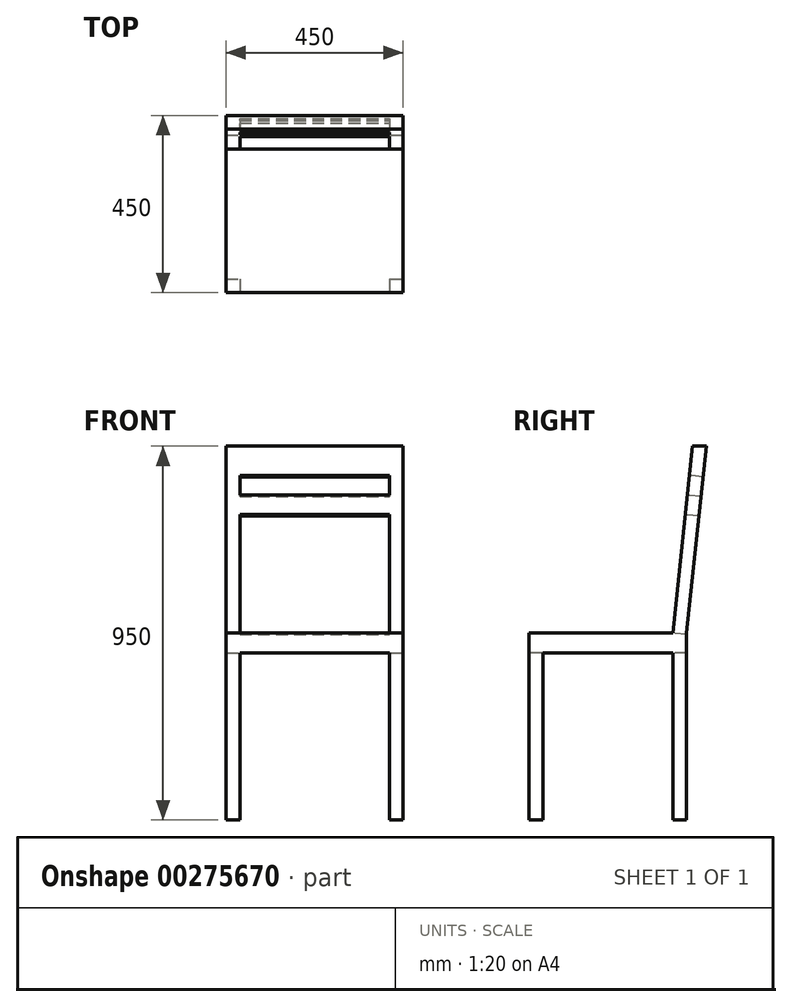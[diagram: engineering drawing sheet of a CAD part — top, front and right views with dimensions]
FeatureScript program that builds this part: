
annotation { "Feature Type Name" : "Feature", "Feature Type Description" : "" }
export const myFeature = defineFeature(function(context is Context, id is Id, definition is map)
    precondition{}
    {
        {
            var Q0;
            Q0=qCreatedBy(makeId("Top.planeOp"),FACE);
            var sketch = newSketch(context, id + "F0", { "sketchPlane" : qUnion([Q0])});
            skLineSegment(sketch, "E0.bottom", {"start": v(225, 225) * mm, "end": v(-225, 225) * mm});
            skLineSegment(sketch, "E0.top", {"start": v(225, -225) * mm, "end": v(-225, -225) * mm});
            skLineSegment(sketch, "E0.left", {"start": v(225, 225) * mm, "end": v(225, -225) * mm});
            skLineSegment(sketch, "E0.right", {"start": v(-225, 225) * mm, "end": v(-225, -225) * mm});
            skPoint(sketch, "E0.middle", {"position": v(0, 0) * mm});
            skSolve(sketch);
        }
        {
            var Q0;
            Q0=qSketchRegion(id+"F0",true);
            extrude(context, id + "F1", {"entities" : qUnion([Q0]), "depth" : 950 * mm});
        }
        {
            var Q0;
            Q0=makeQuery(id+"F1.opExtrude","SWEPT_FACE",FACE,{"disambiguationData":[OSD([sQuery(id+"F0.wireOp",EDGE,"E0.left")])]});
            var sketch = newSketch(context, id + "F2", { "sketchPlane" : qUnion([Q0])});
            skLineSegment(sketch, "E1.bottom", {"start": v(225, 475) * mm, "end": v(-225, 475) * mm});
            skLineSegment(sketch, "E1.top", {"start": v(225, 425) * mm, "end": v(-225, 425) * mm});
            skLineSegment(sketch, "E1.left", {"start": v(225, 475) * mm, "end": v(225, 425) * mm});
            skLineSegment(sketch, "E1.right", {"start": v(-225, 475) * mm, "end": v(-225, 425) * mm});
            skLineSegment(sketch, "E2", {"start": v(225, 950) * mm, "end": v(175, 475) * mm});
            skLineSegment(sketch, "E3", {"start": v(190, 950) * mm, "end": v(140, 475) * mm});
            skLineSegment(sketch, "E4", {"start": v(175, 475) * mm, "end": v(175, 0) * mm});
            skLineSegment(sketch, "E5", {"start": v(140, 475) * mm, "end": v(140, 0) * mm});
            skLineSegment(sketch, "E6", {"start": v(-190, 425) * mm, "end": v(-190, 0) * mm});
            skSolve(sketch);
        }
        {
            var Q0;
            {var subQ0=sQuery(id+"F2.wireOp",EDGE,"E1.left");Q0=makeQuery(id+"F2.imprint","IMPRINT",FACE,{"disambiguationData":[TD([[makeQuery(id+"F2.imprint","IMPRINT",EDGE,{"derivedFrom":subQ0}),-1.0]])]});}
            var Q1;
            {var subQ4=sQuery(id+"F2.wireOp",EDGE,"E2");Q1=makeQuery(id+"F2.imprint","IMPRINT",FACE,{"disambiguationData":[TD([[makeQuery(id+"F2.imprint","IMPRINT",EDGE,{"derivedFrom":subQ4}),1.0]])]});}
            var Q2;
            {var subQ1=sQuery(id+"F0.wireOp",EDGE,"E0.left");var subQ4=sQuery(id+"F2.wireOp",EDGE,"E4");var subQ6=makeQuery(id+"F1.opExtrude","CAP_EDGE",EDGE,{"disambiguationData":[OSD([subQ1])],"isStart":true});var subQ8=makeQuery(id+"F2.imprint","INTERSECT",VERTEX,{"derivedFrom":[subQ6,subQ4]});Q2=makeQuery(id+"F2.imprint","IMPRINT",FACE,{"disambiguationData":[TD([[makeQuery(id+"F2.imprint","IMPRINT",EDGE,{"disambiguationData":[TD([[subQ8,1.0]])],"derivedFrom":subQ4}),1.0]])]});}
            var Q3;
            {var subQ0=sQuery(id+"F2.wireOp",EDGE,"E6");Q3=makeQuery(id+"F2.imprint","IMPRINT",FACE,{"disambiguationData":[TD([[makeQuery(id+"F2.imprint","IMPRINT",EDGE,{"derivedFrom":subQ0}),1.0]])]});}
            var Q4;
            {var subQ4=sQuery(id+"F2.wireOp",EDGE,"E3");Q4=makeQuery(id+"F2.imprint","IMPRINT",FACE,{"disambiguationData":[TD([[makeQuery(id+"F2.imprint","IMPRINT",EDGE,{"derivedFrom":subQ4}),-1.0]])]});}
            extrude(context, id + "F3", {"entities" : qUnion([Q0, Q1, Q2, Q3, Q4]), "operationType" : NewBodyOperationType.REMOVE, "endBound" : BoundingType.THROUGH_ALL, "oppositeDirection" : true, "depth" : 25 * mm});
        }
        {
            var Q0;
            Q0=makeQuery(id+"F1.opExtrude","SWEPT_FACE",FACE,{"disambiguationData":[OSD([sQuery(id+"F0.wireOp",EDGE,"E0.top")])]});
            var sketch = newSketch(context, id + "F4", { "sketchPlane" : qUnion([Q0])});
            skLineSegment(sketch, "E7", {"start": v(-190, 0) * mm, "end": v(-190, 425) * mm});
            skLineSegment(sketch, "E8", {"start": v(-190, 425) * mm, "end": v(190, 425) * mm});
            skLineSegment(sketch, "E9", {"start": v(190, 425) * mm, "end": v(190, 0) * mm});
            skSolve(sketch);
        }
        {
            var Q0;
            Q0 = qSketchRegion(id + "F4", true);
            var Q1;
            {var subQ0=sQuery(id+"F4.wireOp",EDGE,"E7");Q1=makeQuery(id+"F4.imprint","IMPRINT",FACE,{"disambiguationData":[TD([[makeQuery(id+"F4.imprint","IMPRINT",EDGE,{"derivedFrom":subQ0}),-1.0]])]});}
            extrude(context, id + "F5", {"entities" : qUnion([Q0, Q1]), "operationType" : NewBodyOperationType.REMOVE, "endBound" : BoundingType.THROUGH_ALL, "oppositeDirection" : true, "depth" : 25 * mm});
        }
        {
            var Q0;
            Q0=makeQuery(id+"F3.boolean.opBoolean","COPY",FACE,{"derivedFrom":makeQuery(id+"F3.opExtrude","SWEPT_FACE",FACE,{"disambiguationData":[OSD([sQuery(id+"F2.wireOp",EDGE,"E3")])]})});
            var sketch = newSketch(context, id + "F6", { "sketchPlane" : qUnion([Q0])});
            skLineSegment(sketch, "E10", {"start": v(-190, 487.05) * mm, "end": v(-190, 889.67) * mm});
            skLineSegment(sketch, "E11", {"start": v(-190, 889.67) * mm, "end": v(190, 889.67) * mm});
            skLineSegment(sketch, "E12", {"start": v(190, 889.67) * mm, "end": v(190, 487.05) * mm});
            skLineSegment(sketch, "E13", {"start": v(-190, 839.67) * mm, "end": v(190, 839.67) * mm});
            skLineSegment(sketch, "E14", {"start": v(-190, 789.67) * mm, "end": v(190, 789.67) * mm});
            skSolve(sketch);
        }
        {
            var Q0;
            {var subQ0=sQuery(id+"F6.wireOp",EDGE,"E11");Q0=makeQuery(id+"F6.imprint","IMPRINT",FACE,{"disambiguationData":[TD([[makeQuery(id+"F6.imprint","IMPRINT",EDGE,{"derivedFrom":subQ0}),-1.0]])]});}
            var Q1;
            {var subQ3=sQuery(id+"F6.wireOp",EDGE,"E14");Q1=makeQuery(id+"F6.imprint","IMPRINT",FACE,{"disambiguationData":[TD([[makeQuery(id+"F6.imprint","IMPRINT",EDGE,{"derivedFrom":subQ3}),-1.0]])]});}
            extrude(context, id + "F7", {"entities" : qUnion([Q0, Q1]), "operationType" : NewBodyOperationType.REMOVE, "oppositeDirection" : true, "depth" : 25 * mm});
        }
        {
            var Q0;
            Q0=makeQuery(id+"F7.boolean.opBoolean","COPY",FACE,{"derivedFrom":makeQuery(id+"F7.opExtrude","CAP_FACE",FACE,{"disambiguationData":[OSD([sQuery(id+"F6.wireOp",EDGE,"E10"),sQuery(id+"F6.wireOp",EDGE,"E11"),sQuery(id+"F6.wireOp",EDGE,"E12"),sQuery(id+"F6.wireOp",EDGE,"E13")])],"isStart":false})});
            var Q1;
            Q1=makeQuery(id+"F7.boolean.opBoolean","COPY",FACE,{"derivedFrom":makeQuery(id+"F7.opExtrude","CAP_FACE",FACE,{"disambiguationData":[OSD([sQuery(id+"F2.wireOp",EDGE,"E1.bottom"),sQuery(id+"F2.wireOp",EDGE,"E3"),sQuery(id+"F2.wireOp",EDGE,"E5"),sQuery(id+"F6.wireOp",EDGE,"E10"),sQuery(id+"F6.wireOp",EDGE,"E12"),sQuery(id+"F6.wireOp",EDGE,"E14")])],"isStart":false})});
            extrude(context, id + "F8", {"entities" : qUnion([Q0, Q1]), "operationType" : NewBodyOperationType.REMOVE, "endBound" : BoundingType.THROUGH_ALL, "oppositeDirection" : true, "depth" : 25 * mm});
        }
    });
